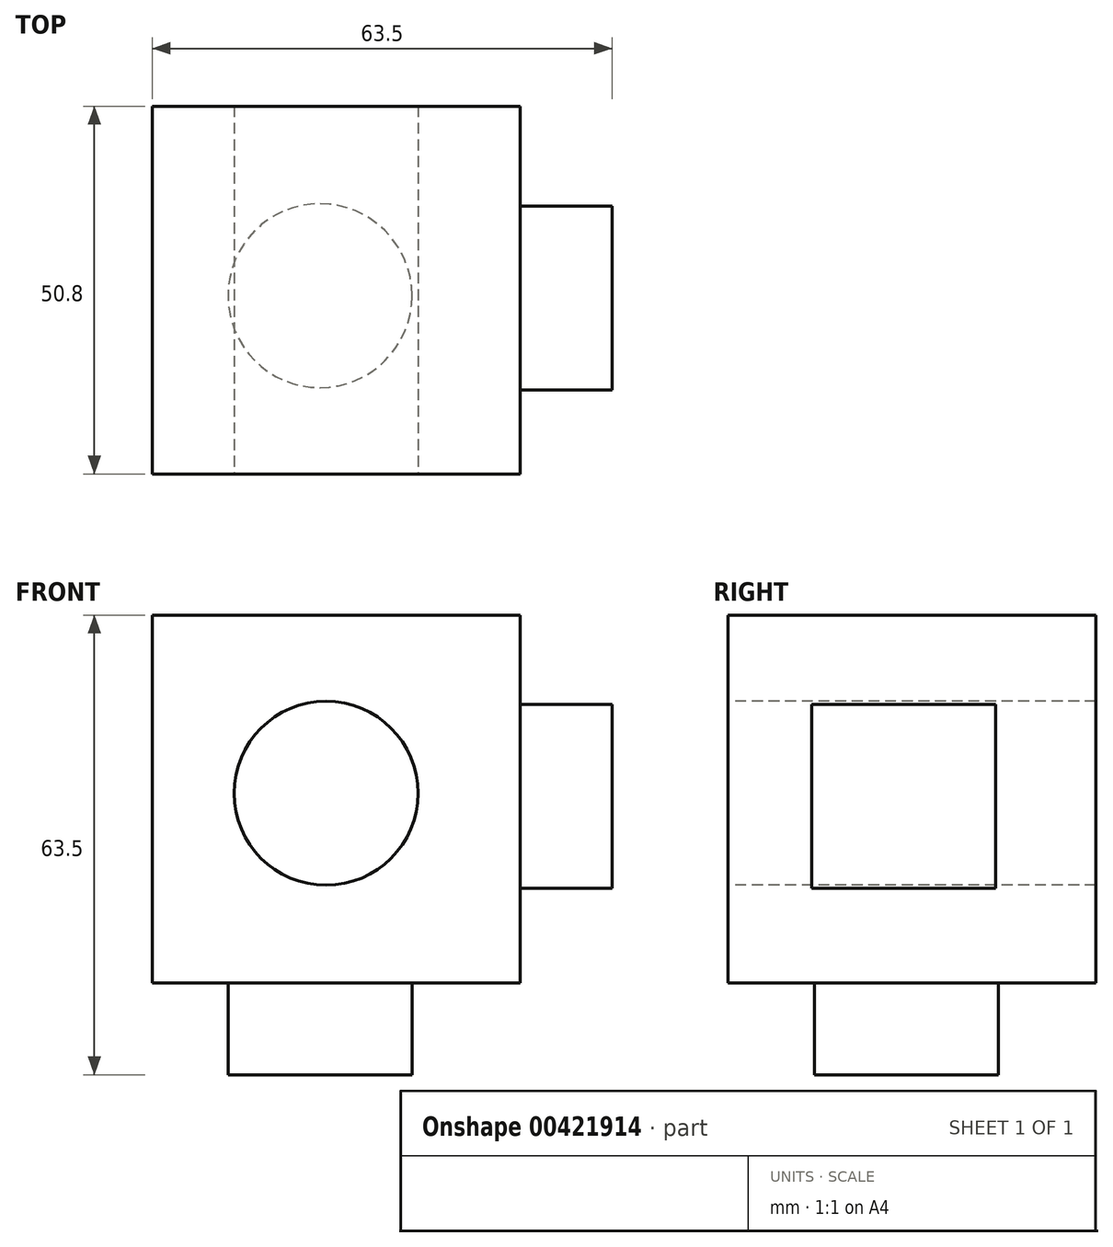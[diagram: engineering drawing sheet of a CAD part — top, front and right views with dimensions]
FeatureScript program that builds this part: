
annotation { "Feature Type Name" : "Feature", "Feature Type Description" : "" }
export const myFeature = defineFeature(function(context is Context, id is Id, definition is map)
    precondition{}
    {
        {
            var Q0;
            Q0=qCreatedBy(makeId("Front.planeOp"),FACE);
            var sketch = newSketch(context, id + "F0", { "sketchPlane" : qUnion([Q0])});
            skLineSegment(sketch, "E0", {"start": v(0, 0) * mm, "end": v(-50.8, 0) * mm});
            skLineSegment(sketch, "E1", {"start": v(0, 0) * mm, "end": v(0, 50.8) * mm});
            skLineSegment(sketch, "E2", {"start": v(0, 50.8) * mm, "end": v(-50.8, 50.8) * mm});
            skLineSegment(sketch, "E3", {"start": v(-50.8, 0) * mm, "end": v(-50.8, 50.8) * mm});
            skSolve(sketch);
        }
        {
            var Q0;
            Q0=makeQuery(id+"F0.imprint","IMPRINT",FACE,{"disambiguationData":[TD([[makeQuery(id+"F0.imprint","IMPRINT",EDGE,{"derivedFrom":sQuery(id+"F0.wireOp",EDGE,"E0")}),-1.0]])]});
            extrude(context, id + "F1", {"entities" : qUnion([Q0]), "depth" : 50.8 * mm});
        }
        {
            var Q0;
            Q0=makeQuery(id+"F1.opExtrude","CAP_FACE",FACE,{"disambiguationData":[OSD([sQuery(id+"F0.wireOp",EDGE,"E0"),sQuery(id+"F0.wireOp",EDGE,"E1"),sQuery(id+"F0.wireOp",EDGE,"E2"),sQuery(id+"F0.wireOp",EDGE,"E3")])],"isStart":false});
            var sketch = newSketch(context, id + "F2", { "sketchPlane" : qUnion([Q0])});
            skCircle(sketch, "E4", {"center": v(-26.8, 26.18) * mm, "radius": 12.7 * mm});
            skSolve(sketch);
        }
        {
            var Q0;
            Q0=makeQuery(id+"F2.imprint","IMPRINT",FACE,{"disambiguationData":[TD([[makeQuery(id+"F2.imprint","IMPRINT",EDGE,{"derivedFrom":sQuery(id+"F2.wireOp",EDGE,"E4")}),1.0]])]});
            extrude(context, id + "F3", {"entities" : qUnion([Q0]), "operationType" : NewBodyOperationType.REMOVE, "oppositeDirection" : true, "depth" : 50.8 * mm});
        }
        {
            var Q0;
            Q0=makeQuery(id+"F1.opExtrude","SWEPT_FACE",FACE,{"disambiguationData":[OSD([sQuery(id+"F0.wireOp",EDGE,"E0")])]});
            var sketch = newSketch(context, id + "F4", { "sketchPlane" : qUnion([Q0])});
            skCircle(sketch, "E5", {"center": v(-27.65, 26.18) * mm, "radius": 12.7 * mm});
            skSolve(sketch);
        }
        {
            var Q0;
            Q0=makeQuery(id+"F4.imprint","IMPRINT",FACE,{"disambiguationData":[TD([[makeQuery(id+"F4.imprint","IMPRINT",EDGE,{"derivedFrom":sQuery(id+"F4.wireOp",EDGE,"E5")}),1.0]])]});
            extrude(context, id + "F5", {"entities" : qUnion([Q0]), "operationType" : NewBodyOperationType.ADD, "depth" : 12.7 * mm});
        }
        {
            var Q0;
            Q0=qCreatedBy(makeId("Right.planeOp"),FACE);
            var sketch = newSketch(context, id + "F6", { "sketchPlane" : qUnion([Q0])});
            skLineSegment(sketch, "E6", {"start": v(-39.23, 13.08) * mm, "end": v(-13.83, 13.08) * mm});
            skLineSegment(sketch, "E7", {"start": v(-39.23, 13.08) * mm, "end": v(-39.23, 38.48) * mm});
            skLineSegment(sketch, "E8", {"start": v(-39.23, 38.48) * mm, "end": v(-13.83, 38.48) * mm});
            skLineSegment(sketch, "E9", {"start": v(-13.83, 38.48) * mm, "end": v(-13.83, 13.08) * mm});
            skSolve(sketch);
        }
        {
            var Q0;
            Q0=makeQuery(id+"F6.imprint","IMPRINT",FACE,{"disambiguationData":[TD([[makeQuery(id+"F6.imprint","IMPRINT",EDGE,{"derivedFrom":sQuery(id+"F6.wireOp",EDGE,"E6")}),1.0]])]});
            extrude(context, id + "F7", {"entities" : qUnion([Q0]), "operationType" : NewBodyOperationType.ADD, "depth" : 12.7 * mm});
        }
    });
